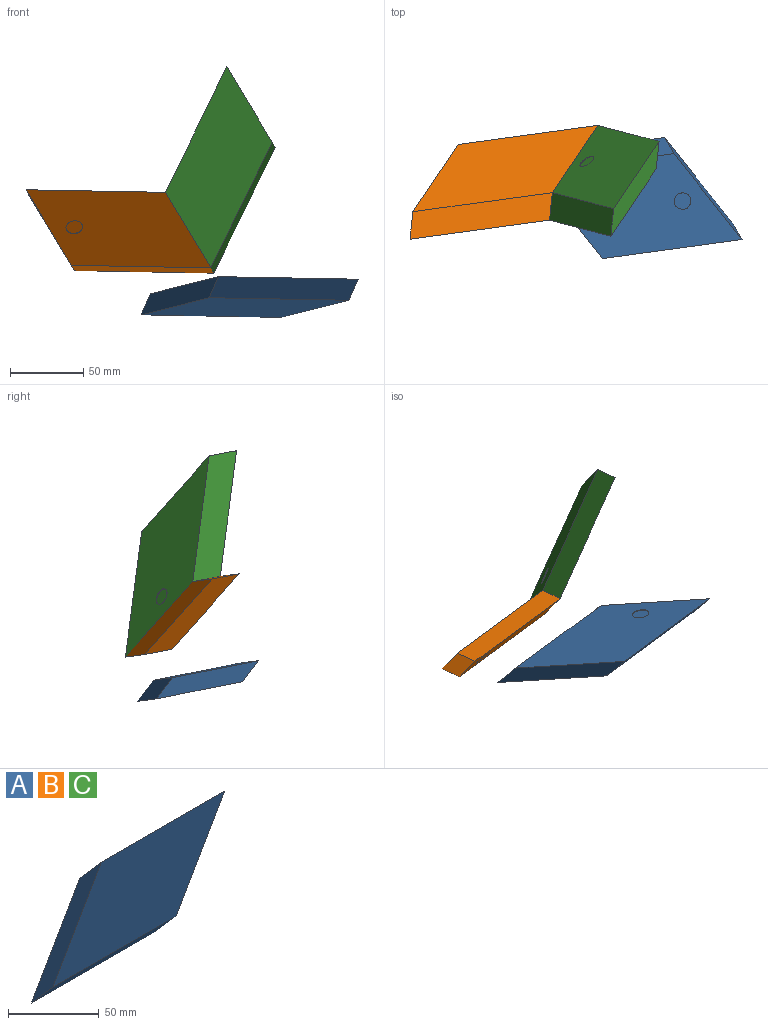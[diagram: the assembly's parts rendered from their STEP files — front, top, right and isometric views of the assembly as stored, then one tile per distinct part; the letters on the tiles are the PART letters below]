
ASSEMBLY  parts=3 mates=1
PART A: 8 faces, bbox 138.8x12x80 mm
  f0: plane 134.22x65.7mm, normal (0,1,0), area 6223.2mm2, adj f1,f3,f4,f5,f6
  f1: plane 100.83x14.3mm, normal (0,-0.77,-0.64), area 1797.5mm2, adj f0,f2,f3,f4
  f2: plane 134.22x65.7mm, normal (0,-1,0), area 6325.8mm2, adj f1,f3,f4,f5
  f3: plane 80x42.48mm, normal (-0.84,0.26,0.48), area 942.5mm2, adj f0,f1,f2,f5
  f4: plane 80x42.48mm, normal (0.84,-0.26,-0.48), area 942.5mm2, adj f0,f1,f2,f5
  f5: plane 100.83x14.3mm, normal (0,0.77,0.64), area 1797.5mm2, adj f0,f2,f3,f4
  f6: cylinder r=5.72mm len=11.43mm, axis (0,1,0), area 18mm2, adj f0,f7
  f7: plane 11.43x11.43mm, normal (0,1,0), area 102.6mm2, adj f6
PART B: same geometry as A
PART C: same geometry as A
PLACE A rot(axis=(0.05,-0.77,-0.64),174.3deg) t=(145.15,-98.44,-36.62)mm
PLACE B rot(axis=(-1,-0.06,0.03),141deg) t=(-89.23,-99.26,24.65)mm fixed
PLACE C rot(axis=(0.51,-0.83,0.22),76.4deg) t=(41.23,-20.44,-35.72)mm
MATE fastened B.f4 <-> C.f3  axis (0.85,0.01,0.52) through (26.34,-53.3,-4.78)mm
